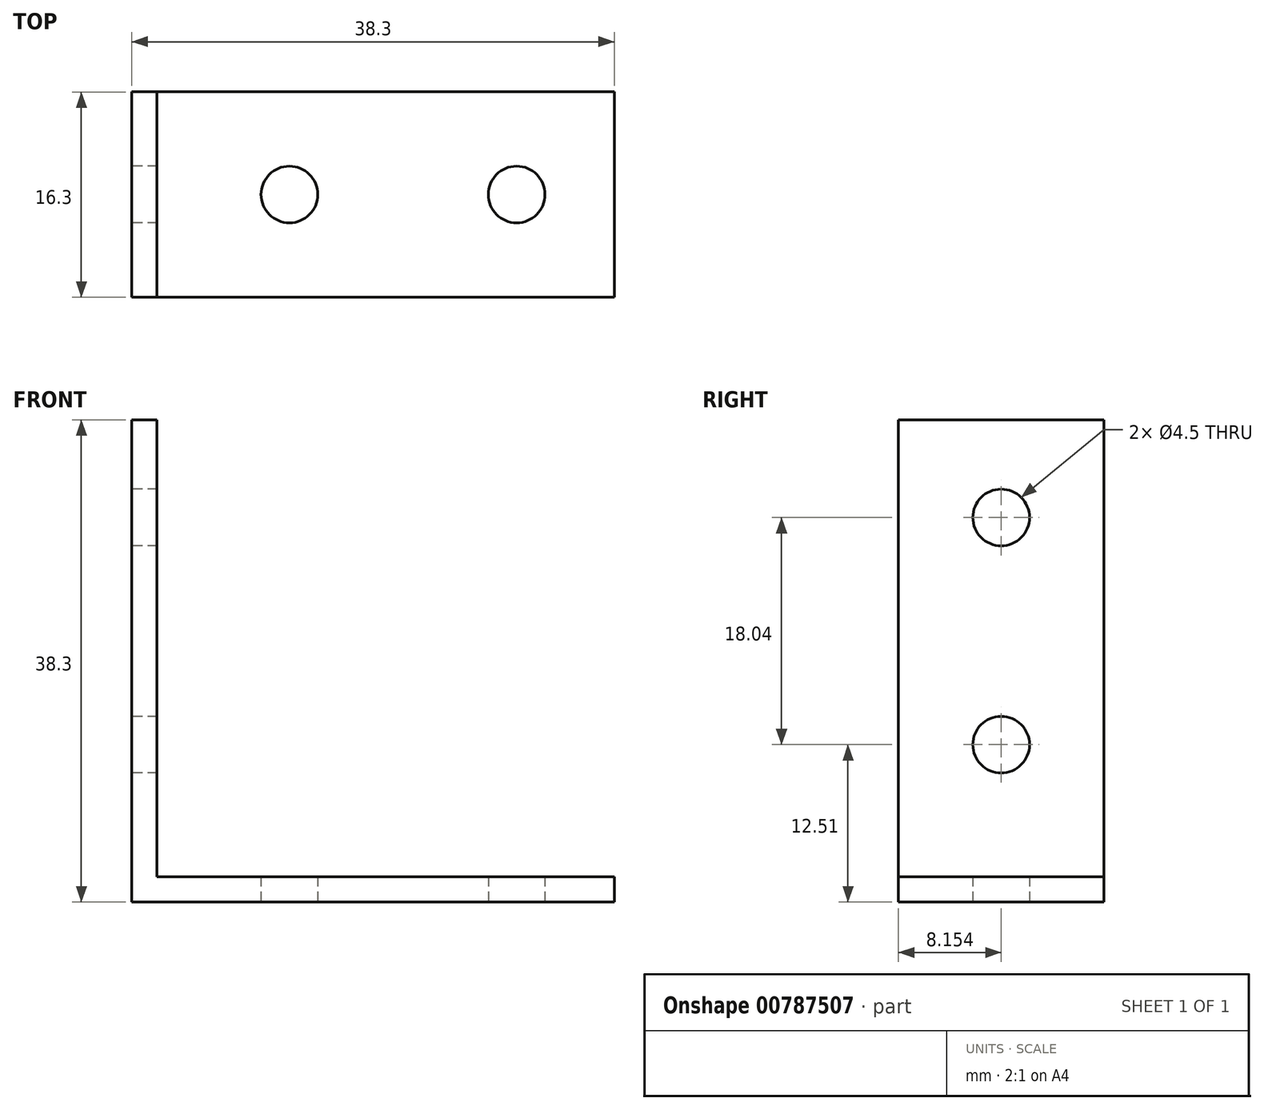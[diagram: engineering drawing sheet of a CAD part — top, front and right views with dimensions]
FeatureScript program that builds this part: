
annotation { "Feature Type Name" : "Feature", "Feature Type Description" : "" }
export const myFeature = defineFeature(function(context is Context, id is Id, definition is map)
    precondition{}
    {
        {
            var Q0;
            Q0=qCreatedBy(makeId("Top.planeOp"),FACE);
            var sketch = newSketch(context, id + "F0", { "sketchPlane" : qUnion([Q0])});
            skLineSegment(sketch, "E0.bottom", {"start": v(-51.02, 51.57) * mm, "end": v(-12.72, 51.57) * mm});
            skLineSegment(sketch, "E0.top", {"start": v(-51.02, 35.27) * mm, "end": v(-12.72, 35.27) * mm});
            skLineSegment(sketch, "E0.left", {"start": v(-51.02, 51.57) * mm, "end": v(-51.02, 35.27) * mm});
            skLineSegment(sketch, "E0.right", {"start": v(-12.72, 51.57) * mm, "end": v(-12.72, 35.27) * mm});
            skCircle(sketch, "E1", {"center": v(-20.47, 43.42) * mm, "radius": 2.25 * mm});
            skPoint(sketch, "E1.centerSnap0", {"position": v(-12.72, 43.42) * mm});
            skCircle(sketch, "E2", {"center": v(-38.51, 43.42) * mm, "radius": 2.25 * mm});
            skSolve(sketch);
        }
        {
            var Q0;
            Q0=makeQuery(id+"F0.imprint","IMPRINT",FACE,{"disambiguationData":[TD([[makeQuery(id+"F0.imprint","IMPRINT",EDGE,{"derivedFrom":sQuery(id+"F0.wireOp",EDGE,"E0.bottom")}),-1.0]])]});
            extrude(context, id + "F1", {"entities" : qUnion([Q0]), "depth" : 2 * mm, "offsetDistance" : 25.4 * mm});
        }
        {
            var Q0;
            Q0=makeQuery(id+"F1.opExtrude","SWEPT_FACE",FACE,{"disambiguationData":[OSD([sQuery(id+"F0.wireOp",EDGE,"E0.left")])]});
            var sketch = newSketch(context, id + "F2", { "sketchPlane" : qUnion([Q0])});
            skLineSegment(sketch, "E3.bottom", {"start": v(-51.57, 0) * mm, "end": v(-51.57, 38.3) * mm});
            skLineSegment(sketch, "E3.top", {"start": v(-35.27, 0) * mm, "end": v(-35.27, 38.3) * mm});
            skLineSegment(sketch, "E3.left", {"start": v(-51.57, 0) * mm, "end": v(-35.27, 0) * mm});
            skLineSegment(sketch, "E3.right", {"start": v(-51.57, 38.3) * mm, "end": v(-35.27, 38.3) * mm});
            skCircle(sketch, "E4", {"center": v(-43.42, 30.55) * mm, "radius": 2.25 * mm});
            skPoint(sketch, "E4.centerSnap0", {"position": v(-43.42, 38.3) * mm});
            skCircle(sketch, "E5", {"center": v(-43.42, 12.5) * mm, "radius": 2.25 * mm});
            skSolve(sketch);
        }
        {
            var Q0;
            {var subQ2=sQuery(id+"F2.wireOp",EDGE,"E3.right");Q0=makeQuery(id+"F2.imprint","IMPRINT",FACE,{"disambiguationData":[TD([[makeQuery(id+"F2.imprint","IMPRINT",EDGE,{"derivedFrom":subQ2}),-1.0]])]});}
            extrude(context, id + "F3", {"entities" : qUnion([Q0]), "operationType" : NewBodyOperationType.ADD, "oppositeDirection" : true, "depth" : 2 * mm, "offsetDistance" : 25.4 * mm});
        }
    });
